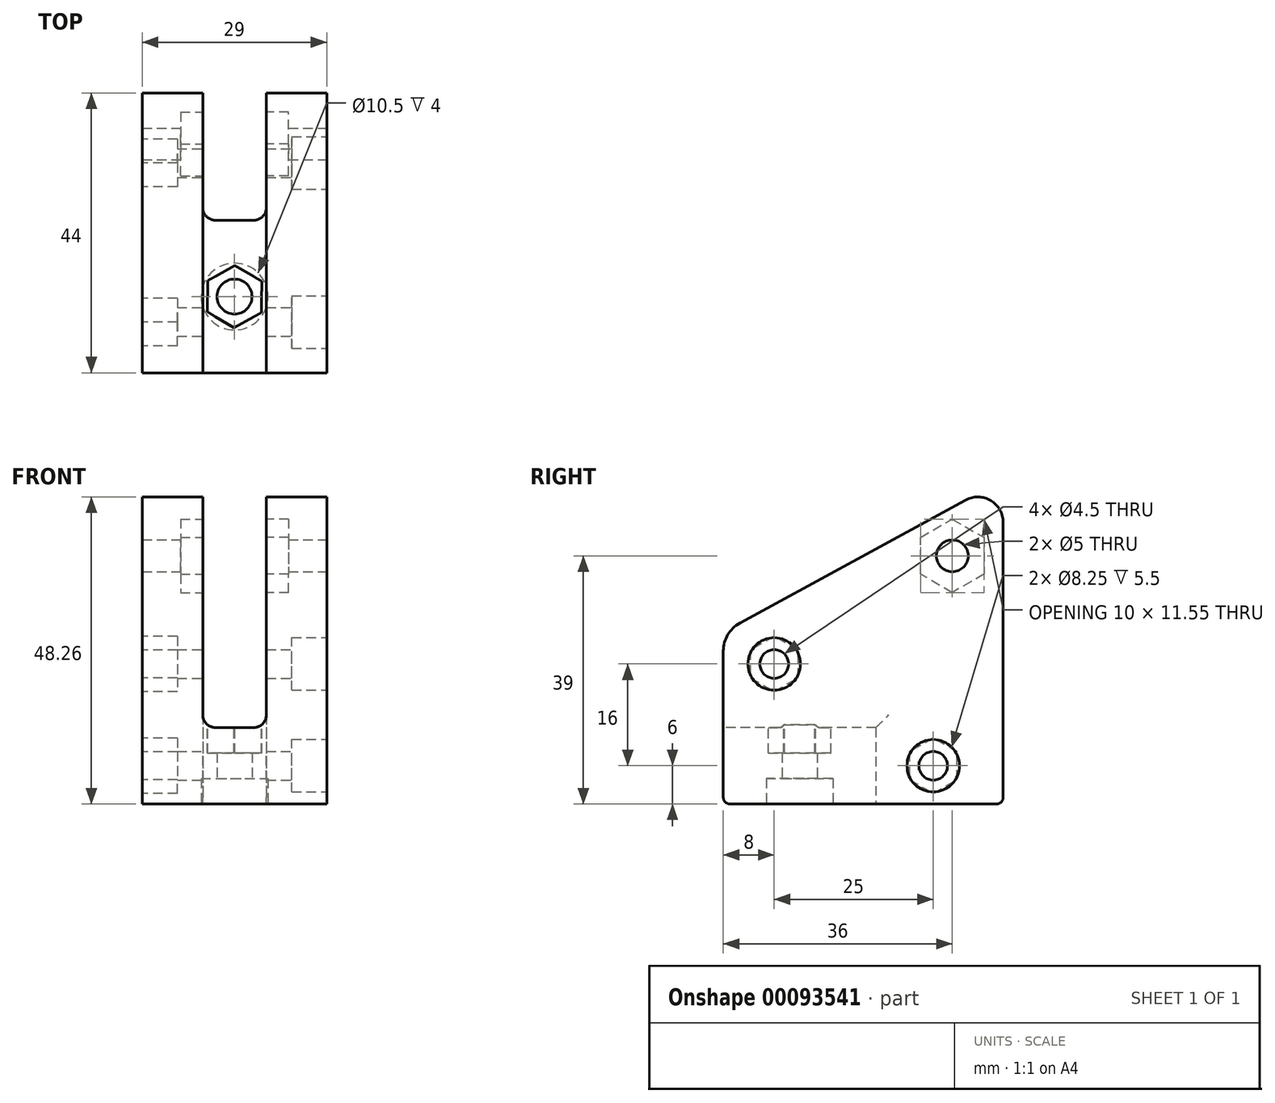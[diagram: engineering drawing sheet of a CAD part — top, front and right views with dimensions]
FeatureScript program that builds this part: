
annotation { "Feature Type Name" : "Feature", "Feature Type Description" : "" }
export const myFeature = defineFeature(function(context is Context, id is Id, definition is map)
    precondition{}
    {
        {
            var Q0;
            Q0=qCreatedBy(makeId("Right.planeOp"),FACE);
            var sketch = newSketch(context, id + "F0", { "sketchPlane" : qUnion([Q0])});
            skLineSegment(sketch, "E0", {"start": v(0, 0) * mm, "end": v(0, 27) * mm});
            skLineSegment(sketch, "E1", {"start": v(0, 27) * mm, "end": v(44, 51) * mm});
            skLineSegment(sketch, "E2", {"start": v(44, 51) * mm, "end": v(44, 0) * mm});
            skLineSegment(sketch, "E3", {"start": v(44, 0) * mm, "end": v(0, 0) * mm});
            skSolve(sketch);
        }
        {
            var Q0;
            Q0 = qSketchRegion(id + "F0", true);
            extrude(context, id + "F1", {"entities" : qUnion([Q0]), "depth" : 29 * mm, "offsetDistance" : 25 * mm});
        }
        {
            var Q0;
            Q0=makeQuery(id+"F1.opExtrude","SWEPT_FACE",FACE,{"disambiguationData":[OSD([sQuery(id+"F0.wireOp",EDGE,"E0")])]});
            var sketch = newSketch(context, id + "F2", { "sketchPlane" : qUnion([Q0])});
            skLineSegment(sketch, "E4", {"start": v(14.5, 0) * mm, "end": v(14.5, 54.56) * mm, "construction": true});
            skLineSegment(sketch, "E5.bottom", {"start": v(9.5, 12) * mm, "end": v(19.5, 12) * mm});
            skLineSegment(sketch, "E5.top", {"start": v(9.5, 62.8) * mm, "end": v(19.5, 62.8) * mm});
            skLineSegment(sketch, "E5.left", {"start": v(9.5, 12) * mm, "end": v(9.5, 62.8) * mm});
            skLineSegment(sketch, "E5.right", {"start": v(19.5, 12) * mm, "end": v(19.5, 62.8) * mm});
            skPoint(sketch, "E6", {"position": v(14.5, 12) * mm});
            skSolve(sketch);
        }
        {
            var Q0;
            Q0 = qSketchRegion(id + "F2", true);
            extrude(context, id + "F3", {"entities" : qUnion([Q0]), "operationType" : NewBodyOperationType.REMOVE, "endBound" : BoundingType.THROUGH_ALL, "oppositeDirection" : true, "depth" : 25 * mm, "offsetDistance" : 25 * mm});
        }
        {
            var Q0;
            Q0=makeQuery(id+"F1.opExtrude","SWEPT_FACE",FACE,{"disambiguationData":[OSD([sQuery(id+"F0.wireOp",EDGE,"E3")])]});
            var sketch = newSketch(context, id + "F4", { "sketchPlane" : qUnion([Q0])});
            skLineSegment(sketch, "E7", {"start": v(14.5, 0) * mm, "end": v(14.5, -62.78) * mm, "construction": true});
            skLineSegment(sketch, "E8.bottom", {"start": v(19.5, -24) * mm, "end": v(9.5, -24) * mm});
            skLineSegment(sketch, "E8.top", {"start": v(19.5, -46.2) * mm, "end": v(9.5, -46.2) * mm});
            skLineSegment(sketch, "E8.left", {"start": v(19.5, -24) * mm, "end": v(19.5, -46.2) * mm});
            skLineSegment(sketch, "E8.right", {"start": v(9.5, -24) * mm, "end": v(9.5, -46.2) * mm});
            skPoint(sketch, "E9", {"position": v(14.5, -24) * mm});
            skSolve(sketch);
        }
        {
            var Q0;
            Q0 = qSketchRegion(id + "F4", true);
            extrude(context, id + "F5", {"entities" : qUnion([Q0]), "operationType" : NewBodyOperationType.REMOVE, "endBound" : BoundingType.THROUGH_ALL, "oppositeDirection" : true, "depth" : 25 * mm, "offsetDistance" : 25 * mm});
        }
        {
            var Q0;
            Q0=makeQuery(id+"F1.opExtrude","SWEPT_FACE",FACE,{"disambiguationData":[OSD([sQuery(id+"F0.wireOp",EDGE,"E3")])]});
            var sketch = newSketch(context, id + "F6", { "sketchPlane" : qUnion([Q0])});
            skLineSegment(sketch, "E10", {"start": v(14.5, 0) * mm, "end": v(14.5, -56.69) * mm, "construction": true});
            skCircle(sketch, "E11", {"center": v(14.5, -12) * mm, "radius": 5.25 * mm});
            skSolve(sketch);
        }
        {
            var Q0;
            Q0 = qSketchRegion(id + "F6", true);
            extrude(context, id + "F7", {"entities" : qUnion([Q0]), "operationType" : NewBodyOperationType.REMOVE, "oppositeDirection" : true, "depth" : 4 * mm, "offsetDistance" : 25 * mm});
        }
        {
            var Q0;
            Q0=makeQuery(id+"F1.opExtrude","CAP_FACE",FACE,{"disambiguationData":[OSD([sQuery(id+"F0.wireOp",EDGE,"E0"),sQuery(id+"F0.wireOp",EDGE,"E1"),sQuery(id+"F0.wireOp",EDGE,"E2"),sQuery(id+"F0.wireOp",EDGE,"E3")])],"isStart":false});
            var sketch = newSketch(context, id + "F8", { "sketchPlane" : qUnion([Q0])});
            skCircle(sketch, "E12", {"center": v(33, 6) * mm, "radius": 2.25 * mm});
            skCircle(sketch, "E13", {"center": v(8, 22) * mm, "radius": 2.25 * mm});
            skCircle(sketch, "E14", {"center": v(36, 39) * mm, "radius": 2.5 * mm});
            skSolve(sketch);
        }
        {
            var Q0;
            Q0 = qSketchRegion(id + "F8", true);
            extrude(context, id + "F9", {"entities" : qUnion([Q0]), "operationType" : NewBodyOperationType.REMOVE, "endBound" : BoundingType.THROUGH_ALL, "oppositeDirection" : true, "depth" : 25 * mm, "offsetDistance" : 25 * mm});
        }
        {
            var Q0;
            {var subQ0=sQuery(id+"F0.wireOp",EDGE,"E3");var subQ1=sQuery(id+"F0.wireOp",EDGE,"E2");Q0=makeQuery(id+"F5.boolean.opBoolean","SPLIT",EDGE,{"disambiguationData":[TD([makeQuery(id+"F3.boolean.opBoolean","COPY",FACE,{"derivedFrom":makeQuery(id+"F3.opExtrude","SWEPT_FACE",FACE,{"disambiguationData":[OSD([sQuery(id+"F2.wireOp",EDGE,"E5.right")])]})})])],"derivedFrom":makeQuery(id+"F1.opExtrude","SWEPT_EDGE",EDGE,{"disambiguationData":[OSD([subQ1,subQ0])]})});}
            var Q1;
            {var subQ0=sQuery(id+"F0.wireOp",EDGE,"E3");var subQ1=sQuery(id+"F0.wireOp",EDGE,"E2");Q1=makeQuery(id+"F5.boolean.opBoolean","SPLIT",EDGE,{"disambiguationData":[TD([makeQuery(id+"F3.boolean.opBoolean","COPY",FACE,{"derivedFrom":makeQuery(id+"F3.opExtrude","SWEPT_FACE",FACE,{"disambiguationData":[OSD([sQuery(id+"F2.wireOp",EDGE,"E5.left")])]})})])],"derivedFrom":makeQuery(id+"F1.opExtrude","SWEPT_EDGE",EDGE,{"disambiguationData":[OSD([subQ1,subQ0])]})});}
            fillet(context, id + "F10", {"entities" : qUnion([Q0, Q1]), "radius" : 1 * mm, "tangentPropagation" : true, "allowEdgeOverflow" : false});
        }
        {
            var Q0;
            {var subQ0=sQuery(id+"F0.wireOp",EDGE,"E0");var subQ1=sQuery(id+"F0.wireOp",EDGE,"E1");Q0=makeQuery(id+"F3.boolean.opBoolean","SPLIT",EDGE,{"disambiguationData":[TD([makeQuery(id+"F3.opExtrude","SWEPT_FACE",FACE,{"disambiguationData":[OSD([sQuery(id+"F2.wireOp",EDGE,"E5.right")])]})])],"derivedFrom":makeQuery(id+"F1.opExtrude","SWEPT_EDGE",EDGE,{"disambiguationData":[OSD([subQ0,subQ1])]})});}
            var Q1;
            {var subQ0=sQuery(id+"F0.wireOp",EDGE,"E0");var subQ1=sQuery(id+"F0.wireOp",EDGE,"E1");Q1=makeQuery(id+"F3.boolean.opBoolean","SPLIT",EDGE,{"disambiguationData":[TD([makeQuery(id+"F3.opExtrude","SWEPT_FACE",FACE,{"disambiguationData":[OSD([sQuery(id+"F2.wireOp",EDGE,"E5.left")])]})])],"derivedFrom":makeQuery(id+"F1.opExtrude","SWEPT_EDGE",EDGE,{"disambiguationData":[OSD([subQ0,subQ1])]})});}
            fillet(context, id + "F11", {"entities" : qUnion([Q0, Q1]), "radius" : 5 * mm, "tangentPropagation" : true, "allowEdgeOverflow" : false});
        }
        {
            var Q0;
            {var subQ0=sQuery(id+"F0.wireOp",EDGE,"E2");var subQ1=sQuery(id+"F0.wireOp",EDGE,"E1");Q0=makeQuery(id+"F3.boolean.opBoolean","SPLIT",EDGE,{"disambiguationData":[TD([makeQuery(id+"F3.opExtrude","SWEPT_FACE",FACE,{"disambiguationData":[OSD([sQuery(id+"F2.wireOp",EDGE,"E5.right")])]})])],"derivedFrom":makeQuery(id+"F1.opExtrude","SWEPT_EDGE",EDGE,{"disambiguationData":[OSD([subQ1,subQ0])]})});}
            var Q1;
            {var subQ0=sQuery(id+"F0.wireOp",EDGE,"E2");var subQ1=sQuery(id+"F0.wireOp",EDGE,"E1");Q1=makeQuery(id+"F3.boolean.opBoolean","SPLIT",EDGE,{"disambiguationData":[TD([makeQuery(id+"F3.opExtrude","SWEPT_FACE",FACE,{"disambiguationData":[OSD([sQuery(id+"F2.wireOp",EDGE,"E5.left")])]})])],"derivedFrom":makeQuery(id+"F1.opExtrude","SWEPT_EDGE",EDGE,{"disambiguationData":[OSD([subQ1,subQ0])]})});}
            fillet(context, id + "F12", {"entities" : qUnion([Q0, Q1]), "radius" : 4 * mm, "tangentPropagation" : true, "allowEdgeOverflow" : false});
        }
        {
            var Q0;
            Q0=makeQuery(id+"F1.opExtrude","CAP_FACE",FACE,{"disambiguationData":[OSD([sQuery(id+"F0.wireOp",EDGE,"E0"),sQuery(id+"F0.wireOp",EDGE,"E1"),sQuery(id+"F0.wireOp",EDGE,"E2"),sQuery(id+"F0.wireOp",EDGE,"E3")])],"isStart":false});
            var sketch = newSketch(context, id + "F13", { "sketchPlane" : qUnion([Q0])});
            skCircle(sketch, "E15", {"center": v(8, 22) * mm, "radius": 4.12 * mm});
            skCircle(sketch, "E16", {"center": v(33, 6) * mm, "radius": 4.12 * mm});
            skSolve(sketch);
        }
        {
            var Q0;
            Q0 = qSketchRegion(id + "F13", true);
            extrude(context, id + "F14", {"entities" : qUnion([Q0]), "operationType" : NewBodyOperationType.REMOVE, "oppositeDirection" : true, "depth" : 5.5 * mm, "offsetDistance" : 25 * mm});
        }
        {
            var Q0;
            Q0=makeQuery(id+"F1.opExtrude","CAP_FACE",FACE,{"disambiguationData":[OSD([sQuery(id+"F0.wireOp",EDGE,"E0"),sQuery(id+"F0.wireOp",EDGE,"E1"),sQuery(id+"F0.wireOp",EDGE,"E2"),sQuery(id+"F0.wireOp",EDGE,"E3")])],"isStart":true});
            var sketch = newSketch(context, id + "F15", { "sketchPlane" : qUnion([Q0])});
            skCircle(sketch, "E17.cCircle", {"center": v(-33, 6) * mm, "radius": 3.75 * mm, "construction": true});
            skLineSegment(sketch, "E17.0", {"start": v(-29.25, 8.17) * mm, "end": v(-29.25, 3.83) * mm});
            skLineSegment(sketch, "E17.1", {"start": v(-29.25, 3.83) * mm, "end": v(-33, 1.67) * mm});
            skLineSegment(sketch, "E17.2", {"start": v(-33, 1.67) * mm, "end": v(-36.75, 3.83) * mm});
            skLineSegment(sketch, "E17.3", {"start": v(-36.75, 3.83) * mm, "end": v(-36.75, 8.17) * mm});
            skLineSegment(sketch, "E17.4", {"start": v(-36.75, 8.17) * mm, "end": v(-33, 10.33) * mm});
            skLineSegment(sketch, "E17.5", {"start": v(-33, 10.33) * mm, "end": v(-29.25, 8.17) * mm});
            skPoint(sketch, "E17.0.midPoint", {"position": v(-29.25, 6) * mm});
            skCircle(sketch, "E18.cCircle", {"center": v(-8, 22) * mm, "radius": 3.75 * mm, "construction": true});
            skLineSegment(sketch, "E18.0", {"start": v(-4.25, 19.83) * mm, "end": v(-8, 17.67) * mm});
            skLineSegment(sketch, "E18.1", {"start": v(-8, 17.67) * mm, "end": v(-11.75, 19.83) * mm});
            skLineSegment(sketch, "E18.2", {"start": v(-11.75, 19.83) * mm, "end": v(-11.75, 24.17) * mm});
            skLineSegment(sketch, "E18.3", {"start": v(-11.75, 24.17) * mm, "end": v(-8, 26.33) * mm});
            skLineSegment(sketch, "E18.4", {"start": v(-8, 26.33) * mm, "end": v(-4.25, 24.17) * mm});
            skLineSegment(sketch, "E18.5", {"start": v(-4.25, 24.17) * mm, "end": v(-4.25, 19.83) * mm});
            skPoint(sketch, "E18.0.midPoint", {"position": v(-6.12, 18.75) * mm});
            skSolve(sketch);
        }
        {
            var Q0;
            Q0 = qSketchRegion(id + "F15", true);
            extrude(context, id + "F16", {"entities" : qUnion([Q0]), "operationType" : NewBodyOperationType.REMOVE, "oppositeDirection" : true, "depth" : 5.5 * mm, "offsetDistance" : 25 * mm});
        }
        {
            var Q0;
            Q0=makeQuery(id+"F7.boolean.opBoolean","COPY",FACE,{"derivedFrom":makeQuery(id+"F7.opExtrude","CAP_FACE",FACE,{"disambiguationData":[OSD([sQuery(id+"F6.wireOp",EDGE,"E11")])],"isStart":false})});
            var sketch = newSketch(context, id + "F17", { "sketchPlane" : qUnion([Q0])});
            skCircle(sketch, "E19", {"center": v(14.5, -12) * mm, "radius": 2.75 * mm});
            skSolve(sketch);
        }
        {
            var Q0;
            Q0 = qSketchRegion(id + "F17", true);
            extrude(context, id + "F18", {"entities" : qUnion([Q0]), "operationType" : NewBodyOperationType.REMOVE, "endBound" : BoundingType.THROUGH_ALL, "oppositeDirection" : true, "depth" : 25 * mm, "offsetDistance" : 25 * mm});
        }
        {
            var Q0;
            Q0=makeQuery(id+"F3.boolean.opBoolean","COPY",FACE,{"derivedFrom":makeQuery(id+"F3.opExtrude","SWEPT_FACE",FACE,{"disambiguationData":[OSD([sQuery(id+"F2.wireOp",EDGE,"E5.bottom")])]})});
            var sketch = newSketch(context, id + "F19", { "sketchPlane" : qUnion([Q0])});
            skCircle(sketch, "E20.cCircle", {"center": v(14.5, 12) * mm, "radius": 4.25 * mm, "construction": true});
            skLineSegment(sketch, "E20.0", {"start": v(14.44, 7.1) * mm, "end": v(10.22, 9.6) * mm});
            skLineSegment(sketch, "E20.1", {"start": v(10.22, 9.6) * mm, "end": v(10.28, 14.5) * mm});
            skLineSegment(sketch, "E20.2", {"start": v(10.28, 14.5) * mm, "end": v(14.56, 16.9) * mm});
            skLineSegment(sketch, "E20.3", {"start": v(14.56, 16.9) * mm, "end": v(18.78, 14.4) * mm});
            skLineSegment(sketch, "E20.4", {"start": v(18.78, 14.4) * mm, "end": v(18.72, 9.5) * mm});
            skLineSegment(sketch, "E20.5", {"start": v(18.72, 9.5) * mm, "end": v(14.44, 7.1) * mm});
            skPoint(sketch, "E20.0.midPoint", {"position": v(12.33, 8.35) * mm});
            skSolve(sketch);
        }
        {
            var Q0;
            Q0 = qSketchRegion(id + "F19", true);
            extrude(context, id + "F20", {"entities" : qUnion([Q0]), "operationType" : NewBodyOperationType.REMOVE, "oppositeDirection" : true, "depth" : 4 * mm, "offsetDistance" : 25 * mm});
        }
        {
            var Q0;
            Q0=makeQuery(id+"F5.boolean.opBoolean","COPY",EDGE,{"derivedFrom":makeQuery(id+"F5.opExtrude","SWEPT_EDGE",EDGE,{"disambiguationData":[OSD([sQuery(id+"F4.wireOp",EDGE,"E8.bottom"),sQuery(id+"F4.wireOp",EDGE,"E8.right")])]})});
            var Q1;
            Q1=makeQuery(id+"F5.boolean.opBoolean","COPY",EDGE,{"derivedFrom":makeQuery(id+"F5.opExtrude","SWEPT_EDGE",EDGE,{"disambiguationData":[OSD([sQuery(id+"F4.wireOp",EDGE,"E8.bottom"),sQuery(id+"F4.wireOp",EDGE,"E8.left")])]})});
            fillet(context, id + "F21", {"entities" : qUnion([Q0, Q1]), "radius" : 2 * mm, "tangentPropagation" : true, "allowEdgeOverflow" : false});
        }
        {
            var Q0;
            Q0=makeQuery(id+"F5.boolean.opBoolean","MERGE",FACE,{"derivedFrom":[makeQuery(id+"F3.boolean.opBoolean","COPY",FACE,{"derivedFrom":makeQuery(id+"F3.opExtrude","SWEPT_FACE",FACE,{"disambiguationData":[OSD([sQuery(id+"F2.wireOp",EDGE,"E5.right")])]})}),makeQuery(id+"F5.opExtrude","SWEPT_FACE",FACE,{"disambiguationData":[OSD([sQuery(id+"F4.wireOp",EDGE,"E8.left")])]})]});
            var sketch = newSketch(context, id + "F22", { "sketchPlane" : qUnion([Q0])});
            skCircle(sketch, "E21.cCircle", {"center": v(-36, 39) * mm, "radius": 5 * mm, "construction": true});
            skLineSegment(sketch, "E21.0", {"start": v(-36, 33.23) * mm, "end": v(-41, 36.11) * mm});
            skLineSegment(sketch, "E21.1", {"start": v(-41, 36.11) * mm, "end": v(-41, 41.89) * mm});
            skLineSegment(sketch, "E21.2", {"start": v(-41, 41.89) * mm, "end": v(-36, 44.77) * mm});
            skLineSegment(sketch, "E21.3", {"start": v(-36, 44.77) * mm, "end": v(-31, 41.89) * mm});
            skLineSegment(sketch, "E21.4", {"start": v(-31, 41.89) * mm, "end": v(-31, 36.11) * mm});
            skLineSegment(sketch, "E21.5", {"start": v(-31, 36.11) * mm, "end": v(-36, 33.23) * mm});
            skPoint(sketch, "E21.0.midPoint", {"position": v(-38.5, 34.67) * mm});
            skSolve(sketch);
        }
        {
            var Q0;
            Q0 = qSketchRegion(id + "F22", true);
            extrude(context, id + "F23", {"entities" : qUnion([Q0]), "operationType" : NewBodyOperationType.REMOVE, "oppositeDirection" : true, "depth" : 3.5 * mm, "offsetDistance" : 25 * mm});
        }
        {
            var Q0;
            Q0=makeQuery(id+"F5.boolean.opBoolean","MERGE",FACE,{"derivedFrom":[makeQuery(id+"F3.boolean.opBoolean","COPY",FACE,{"derivedFrom":makeQuery(id+"F3.opExtrude","SWEPT_FACE",FACE,{"disambiguationData":[OSD([sQuery(id+"F2.wireOp",EDGE,"E5.left")])]})}),makeQuery(id+"F5.opExtrude","SWEPT_FACE",FACE,{"disambiguationData":[OSD([sQuery(id+"F4.wireOp",EDGE,"E8.right")])]})]});
            var sketch = newSketch(context, id + "F24", { "sketchPlane" : qUnion([Q0])});
            skCircle(sketch, "E22.cCircle", {"center": v(36, 39) * mm, "radius": 5 * mm, "construction": true});
            skLineSegment(sketch, "E22.0", {"start": v(41, 36.11) * mm, "end": v(36, 33.23) * mm});
            skLineSegment(sketch, "E22.1", {"start": v(36, 33.23) * mm, "end": v(31, 36.11) * mm});
            skLineSegment(sketch, "E22.2", {"start": v(31, 36.11) * mm, "end": v(31, 41.89) * mm});
            skLineSegment(sketch, "E22.3", {"start": v(31, 41.89) * mm, "end": v(36, 44.77) * mm});
            skLineSegment(sketch, "E22.4", {"start": v(36, 44.77) * mm, "end": v(41, 41.89) * mm});
            skLineSegment(sketch, "E22.5", {"start": v(41, 41.89) * mm, "end": v(41, 36.11) * mm});
            skPoint(sketch, "E22.0.midPoint", {"position": v(38.5, 34.67) * mm});
            skSolve(sketch);
        }
        {
            var Q0;
            Q0 = qSketchRegion(id + "F24", true);
            extrude(context, id + "F25", {"entities" : qUnion([Q0]), "operationType" : NewBodyOperationType.REMOVE, "oppositeDirection" : true, "depth" : 3.5 * mm, "offsetDistance" : 25 * mm});
        }
        {
            var Q0;
            Q0=makeQuery(id+"F1.opExtrude","SWEPT_EDGE",EDGE,{"disambiguationData":[OSD([sQuery(id+"F0.wireOp",EDGE,"E0"),sQuery(id+"F0.wireOp",EDGE,"E3")])]});
            fillet(context, id + "F26", {"entities" : qUnion([Q0]), "radius" : 1 * mm, "tangentPropagation" : true, "allowEdgeOverflow" : false});
        }
        {
            var Q0;
            Q0=makeQuery(id+"F3.boolean.opBoolean","COPY",EDGE,{"derivedFrom":makeQuery(id+"F3.opExtrude","SWEPT_EDGE",EDGE,{"disambiguationData":[OSD([sQuery(id+"F2.wireOp",EDGE,"E5.bottom"),sQuery(id+"F2.wireOp",EDGE,"E5.left")])]})});
            var Q1;
            Q1=makeQuery(id+"F3.boolean.opBoolean","COPY",EDGE,{"derivedFrom":makeQuery(id+"F3.opExtrude","SWEPT_EDGE",EDGE,{"disambiguationData":[OSD([sQuery(id+"F2.wireOp",EDGE,"E5.bottom"),sQuery(id+"F2.wireOp",EDGE,"E5.right")])]})});
            fillet(context, id + "F27", {"entities" : qUnion([Q0, Q1]), "radius" : 2 * mm, "tangentPropagation" : true, "allowEdgeOverflow" : false});
        }
    });
